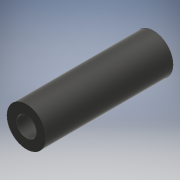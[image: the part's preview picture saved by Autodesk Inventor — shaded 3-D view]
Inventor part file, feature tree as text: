
AUTODESK INVENTOR PART (.ipt)
format: ipt  version: 2017.3 (Build 213256000, 256)  size: 101,376 bytes
history: native  units: mm
features: extrude x1, sketch x1
ambient origin geometry x8: Origin, YZ Plane, XZ Plane, XY Plane, X Axis, Y Axis, Z Axis, Center Point
bodies: Solid1 (feature_tree)
feature tree (2):
  extrude  "Extrusion1"  Depth=20.2mm
  sketch  "Sketch1"  dims[d0=6.2mm d1=3.2mm d2=20.2mm d3=0.0mm]
